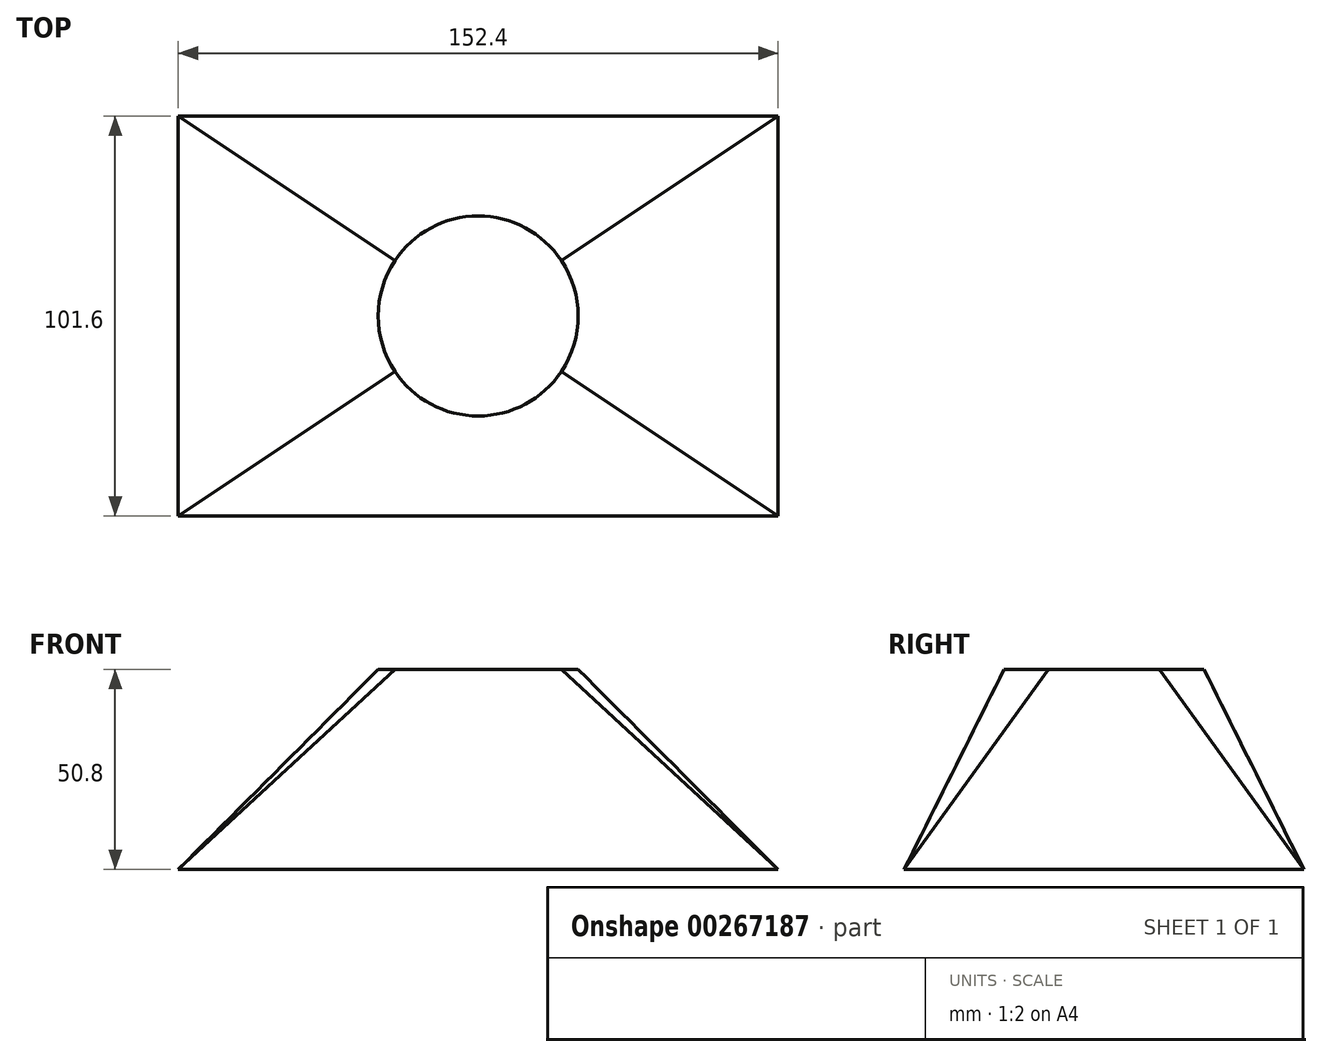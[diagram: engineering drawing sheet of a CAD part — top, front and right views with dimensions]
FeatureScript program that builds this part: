
annotation { "Feature Type Name" : "Feature", "Feature Type Description" : "" }
export const myFeature = defineFeature(function(context is Context, id is Id, definition is map)
    precondition{}
    {
        {
            var Q0;
            Q0=qCreatedBy(makeId("Top.planeOp"),FACE);
            var sketch = newSketch(context, id + "F0", { "sketchPlane" : qUnion([Q0])});
            skLineSegment(sketch, "E0.bottom", {"start": v(-76.2, 50.8) * mm, "end": v(76.2, 50.8) * mm});
            skLineSegment(sketch, "E0.top", {"start": v(-76.2, -50.8) * mm, "end": v(76.2, -50.8) * mm});
            skLineSegment(sketch, "E0.left", {"start": v(-76.2, 50.8) * mm, "end": v(-76.2, -50.8) * mm});
            skLineSegment(sketch, "E0.right", {"start": v(76.2, 50.8) * mm, "end": v(76.2, -50.8) * mm});
            skPoint(sketch, "E0.middle", {"position": v(0, 0) * mm});
            skSolve(sketch);
        }
        {
            var Q0;
            Q0=qCreatedBy(makeId("Top.planeOp"),FACE);
            cPlane(context, id + "F1", {"entities" : qUnion([Q0]), "cplaneType" : CPlaneType.OFFSET, "offset" : 50.8 * mm, "width" : 152.4 * mm, "height" : 152.4 * mm});
        }
        {
            var Q0;
            Q0=qCreatedBy(id+"F1.planeOp",FACE);
            var sketch = newSketch(context, id + "F2", { "sketchPlane" : qUnion([Q0])});
            skPoint(sketch, "E1.0", {"position": v(-76.2, 50.8) * mm});
            skPoint(sketch, "E1.1", {"position": v(76.2, 50.8) * mm});
            skPoint(sketch, "E1.2", {"position": v(76.2, -50.8) * mm});
            skPoint(sketch, "E1.3", {"position": v(-76.2, -50.8) * mm});
            skArc(sketch, "E2", {"start": v(-21.13, 14.09) * mm, "mid": v(-25.4, 0) * mm, "end": v(-21.13, -14.09) * mm});
            skArc(sketch, "E3", {"start": v(21.13, 14.09) * mm, "mid": v(0, 25.4) * mm, "end": v(-21.13, 14.09) * mm});
            skArc(sketch, "E4", {"start": v(21.13, -14.09) * mm, "mid": v(25.4, 0) * mm, "end": v(21.13, 14.09) * mm});
            skArc(sketch, "E5", {"start": v(-21.13, -14.09) * mm, "mid": v(0, -25.4) * mm, "end": v(21.13, -14.09) * mm});
            skLineSegment(sketch, "E6", {"start": v(-76.2, 50.8) * mm, "end": v(0, 0) * mm, "construction": true});
            skLineSegment(sketch, "E7", {"start": v(76.2, 50.8) * mm, "end": v(0, 0) * mm, "construction": true});
            skLineSegment(sketch, "E8", {"start": v(76.2, -50.8) * mm, "end": v(0, 0) * mm, "construction": true});
            skLineSegment(sketch, "E9", {"start": v(-76.2, -50.8) * mm, "end": v(0, 0) * mm, "construction": true});
            skSolve(sketch);
        }
        {
            var Q0;
            Q0=makeQuery(id+"F0.imprint","IMPRINT",FACE,{"disambiguationData":[TD([[makeQuery(id+"F0.imprint","IMPRINT",EDGE,{"derivedFrom":sQuery(id+"F0.wireOp",EDGE,"E0.bottom")}),-1.0]])]});
            var Q1;
            Q1=makeQuery(id+"F2.imprint","IMPRINT",FACE,{"disambiguationData":[TD([[makeQuery(id+"F2.imprint","IMPRINT",EDGE,{"derivedFrom":sQuery(id+"F2.wireOp",EDGE,"E2")}),1.0]])]});
            loft(context, id + "F3", {"sheetProfilesArray" : [{ "sheetProfileEntities" : qUnion([Q0]) }, { "sheetProfileEntities" : qUnion([Q1]) }]});
        }
    });
